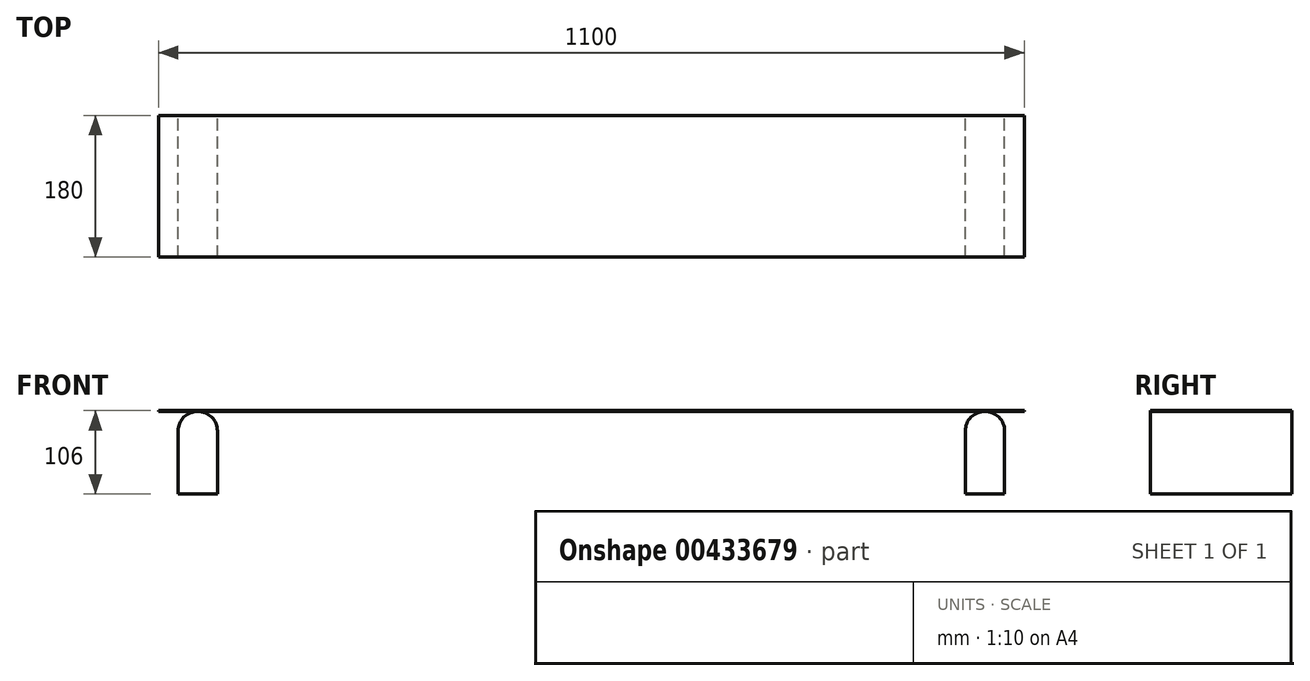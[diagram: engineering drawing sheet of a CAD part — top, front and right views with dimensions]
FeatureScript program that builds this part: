
annotation { "Feature Type Name" : "Feature", "Feature Type Description" : "" }
export const myFeature = defineFeature(function(context is Context, id is Id, definition is map)
    precondition{}
    {
        {
            var Q0;
            Q0=qCreatedBy(makeId("Front.planeOp"),FACE);
            var sketch = newSketch(context, id + "F0", { "sketchPlane" : qUnion([Q0])});
            skLineSegment(sketch, "E0.bottom", {"start": v(0, 0) * mm, "end": v(1100, 0) * mm});
            skLineSegment(sketch, "E0.top", {"start": v(0, 1) * mm, "end": v(1100, 1) * mm});
            skLineSegment(sketch, "E0.left", {"start": v(0, 0) * mm, "end": v(0, 1) * mm});
            skLineSegment(sketch, "E0.right", {"start": v(1100, 0) * mm, "end": v(1100, 1) * mm});
            skArc(sketch, "E1", {"start": v(75, -25) * mm, "mid": v(50, 0) * mm, "end": v(25, -25) * mm});
            skArc(sketch, "E2", {"start": v(1075, -25) * mm, "mid": v(1050, 0) * mm, "end": v(1025, -25) * mm});
            skArc(sketch, "E3", {"start": v(625, 26) * mm, "mid": v(650, 1) * mm, "end": v(675, 26) * mm});
            skArc(sketch, "E4", {"start": v(425, 26) * mm, "mid": v(450, 1) * mm, "end": v(475, 26) * mm});
            skCircle(sketch, "E5", {"center": v(450, 26) * mm, "radius": 25 * mm});
            skCircle(sketch, "E6", {"center": v(650, 26) * mm, "radius": 25 * mm});
            skLineSegment(sketch, "E7.top", {"start": v(25, -105) * mm, "end": v(75, -105) * mm});
            skLineSegment(sketch, "E7.left", {"start": v(25, -25) * mm, "end": v(25, -105) * mm});
            skLineSegment(sketch, "E7.right", {"start": v(75, -25) * mm, "end": v(75, -105) * mm});
            skLineSegment(sketch, "E8.top", {"start": v(1075, -105) * mm, "end": v(1025, -105) * mm});
            skLineSegment(sketch, "E8.left", {"start": v(1075, -25) * mm, "end": v(1075, -105) * mm});
            skLineSegment(sketch, "E8.right", {"start": v(1025, -25) * mm, "end": v(1025, -105) * mm});
            skSolve(sketch);
        }
        {
            var Q0;
            {var subQ0=sQuery(id+"F0.wireOp",EDGE,"E0.left");Q0=makeQuery(id+"F0.imprint","IMPRINT",FACE,{"disambiguationData":[TD([[makeQuery(id+"F0.imprint","IMPRINT",EDGE,{"derivedFrom":subQ0}),-1.0]])]});}
            extrude(context, id + "F1", {"entities" : qUnion([Q0]), "depth" : 180 * mm, "offsetDistance" : 25 * mm});
        }
        {
            var Q0;
            {var subQ0=sQuery(id+"F0.wireOp",EDGE,"E1");Q0=makeQuery(id+"F0.imprint","IMPRINT",FACE,{"disambiguationData":[TD([[makeQuery(id+"F0.imprint","IMPRINT",EDGE,{"disambiguationData":[TD([[makeQuery(id+"F0.imprint","INTERSECT",VERTEX,{"derivedFrom":[sQuery(id+"F0.wireOp",EDGE,"E0.bottom"),subQ0]}),-1.0]])],"derivedFrom":subQ0}),1.0]])]});}
            var Q1;
            {var subQ0=sQuery(id+"F0.wireOp",EDGE,"E5");Q1=makeQuery(id+"F0.imprint","IMPRINT",FACE,{"disambiguationData":[TD([[makeQuery(id+"F0.imprint","IMPRINT",EDGE,{"disambiguationData":[TD([[makeQuery(id+"F0.imprint","INTERSECT",VERTEX,{"derivedFrom":[sQuery(id+"F0.wireOp",EDGE,"E0.top"),subQ0]}),-1.0]])],"derivedFrom":subQ0}),1.0]])]});}
            var Q2;
            {var subQ0=sQuery(id+"F0.wireOp",EDGE,"E6");Q2=makeQuery(id+"F0.imprint","IMPRINT",FACE,{"disambiguationData":[TD([[makeQuery(id+"F0.imprint","IMPRINT",EDGE,{"disambiguationData":[TD([[makeQuery(id+"F0.imprint","INTERSECT",VERTEX,{"derivedFrom":[sQuery(id+"F0.wireOp",EDGE,"E0.top"),subQ0]}),-1.0]])],"derivedFrom":subQ0}),1.0]])]});}
            var Q3;
            {var subQ0=sQuery(id+"F0.wireOp",EDGE,"E2");Q3=makeQuery(id+"F0.imprint","IMPRINT",FACE,{"disambiguationData":[TD([[makeQuery(id+"F0.imprint","IMPRINT",EDGE,{"disambiguationData":[TD([[makeQuery(id+"F0.imprint","INTERSECT",VERTEX,{"derivedFrom":[sQuery(id+"F0.wireOp",EDGE,"E0.bottom"),subQ0]}),-1.0]])],"derivedFrom":subQ0}),1.0]])]});}
            var Q4;
            Q4=sQuery(id+"F0.wireOp",EDGE,"dae0d0fb-9bb7-4ea1-beea-69520374408a.0");
            extrude(context, id + "F2", {"entities" : qUnion([Q0, Q1, Q2, Q3]), "surfaceEntities" : qUnion([Q4]), "depth" : 180 * mm, "offsetDistance" : 25 * mm});
        }
    });
